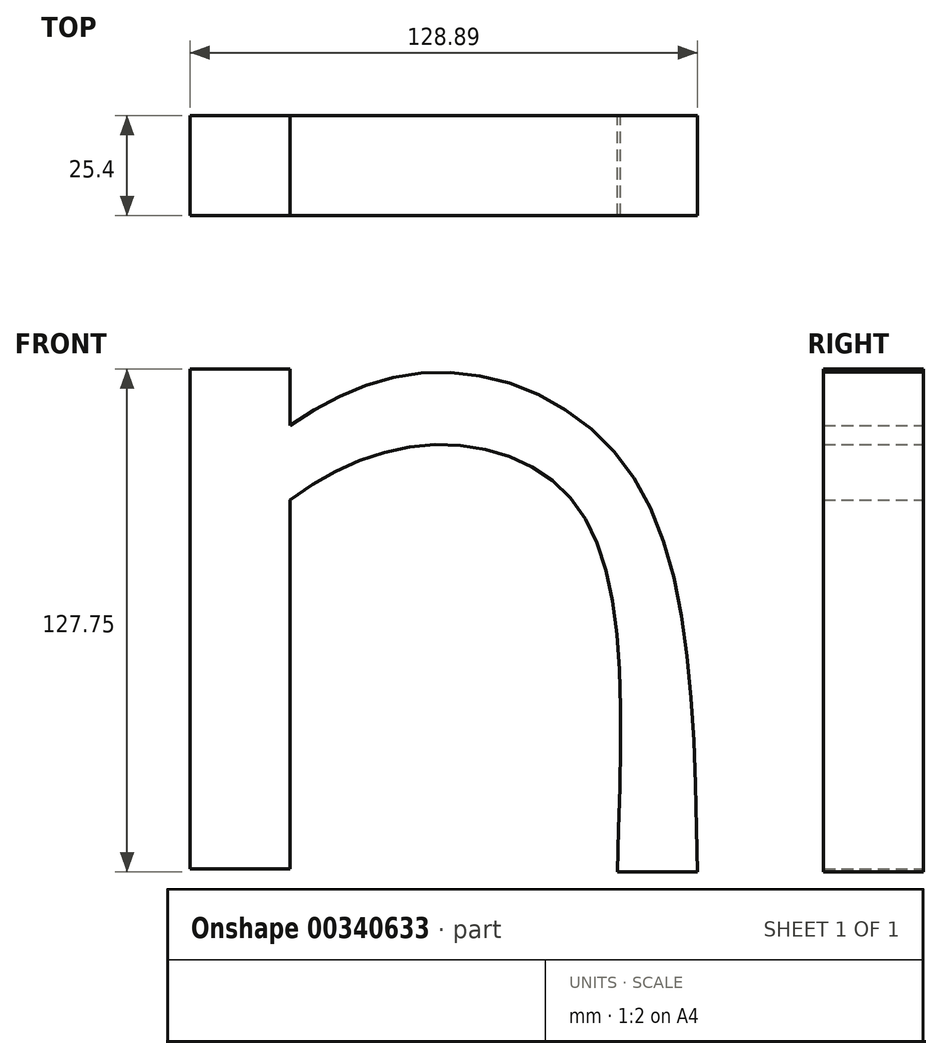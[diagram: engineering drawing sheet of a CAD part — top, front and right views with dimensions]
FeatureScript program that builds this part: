
annotation { "Feature Type Name" : "Feature", "Feature Type Description" : "" }
export const myFeature = defineFeature(function(context is Context, id is Id, definition is map)
    precondition{}
    {
        {
            var Q0;
            Q0=qCreatedBy(makeId("Front.planeOp"),FACE);
            var sketch = newSketch(context, id + "F0", { "sketchPlane" : qUnion([Q0])});
            skLineSegment(sketch, "E0.bottom", {"start": v(-35.33, 63.2) * mm, "end": v(-60.73, 63.2) * mm});
            skLineSegment(sketch, "E0.top", {"start": v(-35.33, -63.8) * mm, "end": v(-60.73, -63.8) * mm});
            skLineSegment(sketch, "E0.left", {"start": v(-35.33, 63.2) * mm, "end": v(-35.33, -63.8) * mm});
            skLineSegment(sketch, "E0.right", {"start": v(-60.73, 63.2) * mm, "end": v(-60.73, -63.8) * mm});
            skFitSpline(sketch, "E1", {"points": [v(-46.1, 40.3) * mm, v(0, 62.38) * mm, v(51.48, 36.4) * mm, v(68.16, -64.54) * mm], "startDerivative": vector(135.67, 119.84) * mm, "endDerivative": vector(6.05, -274.7) * mm});
            skFitSpline(sketch, "E2", {"points": [v(-46.1, 19.98) * mm, v(-0.97, 43.86) * mm, v(38.55, 26.96) * mm, v(47.84, -64.54) * mm], "startDerivative": vector(122.22, 133.69) * mm, "endDerivative": vector(-6.85, -274.6) * mm});
            skLineSegment(sketch, "E3", {"start": v(47.84, -64.54) * mm, "end": v(68.16, -64.54) * mm});
            skLineSegment(sketch, "E4", {"start": v(-46.1, 40.3) * mm, "end": v(-46.1, 19.98) * mm});
            skSolve(sketch);
        }
        {
            var Q0;
            {var subQ4=sQuery(id+"F0.wireOp",EDGE,"E0.bottom");Q0=makeQuery(id+"F0.imprint","IMPRINT",FACE,{"disambiguationData":[TD([[makeQuery(id+"F0.imprint","IMPRINT",EDGE,{"derivedFrom":subQ4}),1.0]])]});}
            extrude(context, id + "F1", {"entities" : qUnion([Q0]), "depth" : 25.4 * mm});
        }
        {
            var Q0;
            {var subQ5=sQuery(id+"F0.wireOp",EDGE,"E3");Q0=makeQuery(id+"F0.imprint","IMPRINT",FACE,{"disambiguationData":[TD([[makeQuery(id+"F0.imprint","IMPRINT",EDGE,{"derivedFrom":subQ5}),1.0]])]});}
            var Q1;
            {var subQ5=sQuery(id+"F0.wireOp",EDGE,"E4");Q1=makeQuery(id+"F0.imprint","IMPRINT",FACE,{"disambiguationData":[TD([[makeQuery(id+"F0.imprint","IMPRINT",EDGE,{"derivedFrom":subQ5}),1.0]])]});}
            extrude(context, id + "F2", {"entities" : qUnion([Q0, Q1]), "operationType" : NewBodyOperationType.ADD, "depth" : 25.4 * mm});
        }
    });
